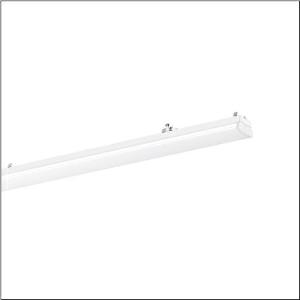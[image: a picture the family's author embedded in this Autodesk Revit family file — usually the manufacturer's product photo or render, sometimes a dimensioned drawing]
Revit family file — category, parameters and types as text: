
# Revit family: licross_21_recessed_opal_ho_52tl1dcn4cxm
name_source: partatom
category: Lighting Fixtures
units: mm (PartAtom-declared; Revit-internal decimal feet)

## family parameters
Cut with Voids When Loaded = No
Host = Face
Light Source = No
Part Type = Normal
Room Calculation Point = No
Round Connector Dimension = Use Diameter
Shared = No

## types (1)
- --- (1 x LED, 12300 lm, 68.4 W, 4000K)
    Apparent Load = 68 VA
    CIE Flux Codes = 44 73 91 87 100
    Color Rendering = 80
    Color Temperature = 4000K
    Default Elevation = 1800 mm
    Description = Licross 21 recessed opal HO, luminaire insert, of sheet steel, galvanised, coil coated, white, length: 1.500mm, width: 66mm, height: 67mm, LED rated luminous flux: 12.300lm, light colour: 840, SDCM (Standard Deviation of Colour Matching)MacAdam ≤ 3 SDCM (initial), control gear: ON/OFF Multilumen, CLOi, with plug, 3-pole, with phase selection, mains connection: 220..240V, AC, 50/60Hz, start of lifetime: 68W, end of service life: 83W, internal wiring halogen-free, primary optical cover: cover, of PMMA, light emission: direct with ceiling illumination distribution, primary light characteristic: symmetric, protection rating (complete): IP40, insulation class (complete): insulation class I (protective earthing), certification: CE, ENEC, VDE, UKCA, protection symbol: D if used in an environment without relevant dust loads with corresponding accessories, impact resistance: IK06, permissible ambient temperature for indoor applications: -35..+30°C, corresponds to IFS (International Featured Standards) requirements for safety and quality in the food industry, reducing of maximum allowable ambient temperature of 5°C with ceiling mounting, LABS conformity tested according to VDMA 24364:2018-05, The light source and the operating device comply with the requirements of the Ecodesign Regulation (EU) 2019/2020 and are replaceable in accordance with this regulation, packaging unit: 1 piece
    Height = 83 mm
    Lamp = 1 x LED
    Lamp Light Flux = 12300 lm
    Lamp Power = 68.4 W
    Lamp count = 1
    Length = 1500 mm
    Luminous efficacy = 180 lm/W
    Manufacturer = Siteco
    ModVariant = No
    Model = 52TL1DCN4CXM
    Mounting Place = Ceiling
    Mounting Type = Pendant
    Number of Poles = 1
    OnlyDefault = Yes
    Power Factor = 1
    Product Name = Licross 21 recessed opal HO
    Product group = luminaire insert | ceiling pendant
    ProductGroupID = 901
    Protection Class = Protection class I
    Protection Degree = IP 40
    RLX_Detail_Level = 1
    RLX_Emergency_Light_Flux = 0 lm
    RLX_Emergency_Type = 0
    RLX_Emergency_Type_DB = No
    RlxData = <blob elided: 25333 chars, md5=42270155>
    Socket = socket
    Standby Power = 0 W
    System Light Flux = 12300 lm
    System Power = 68 W
    Type Comments = factory setting: luminous flux: 100 % | (A | C | E) | 161 mA
    Type Image = l_1313666.jpg
    URL = http://relux.com
    VarID = @adj_077505
    Voltage = 0 V
    Weight = 0.00 kg
    Width = 76 mm

## geometry (parser evidence)
native form markers: Blend x4, Sweep x12
no freeform markers — native parametric forms only
